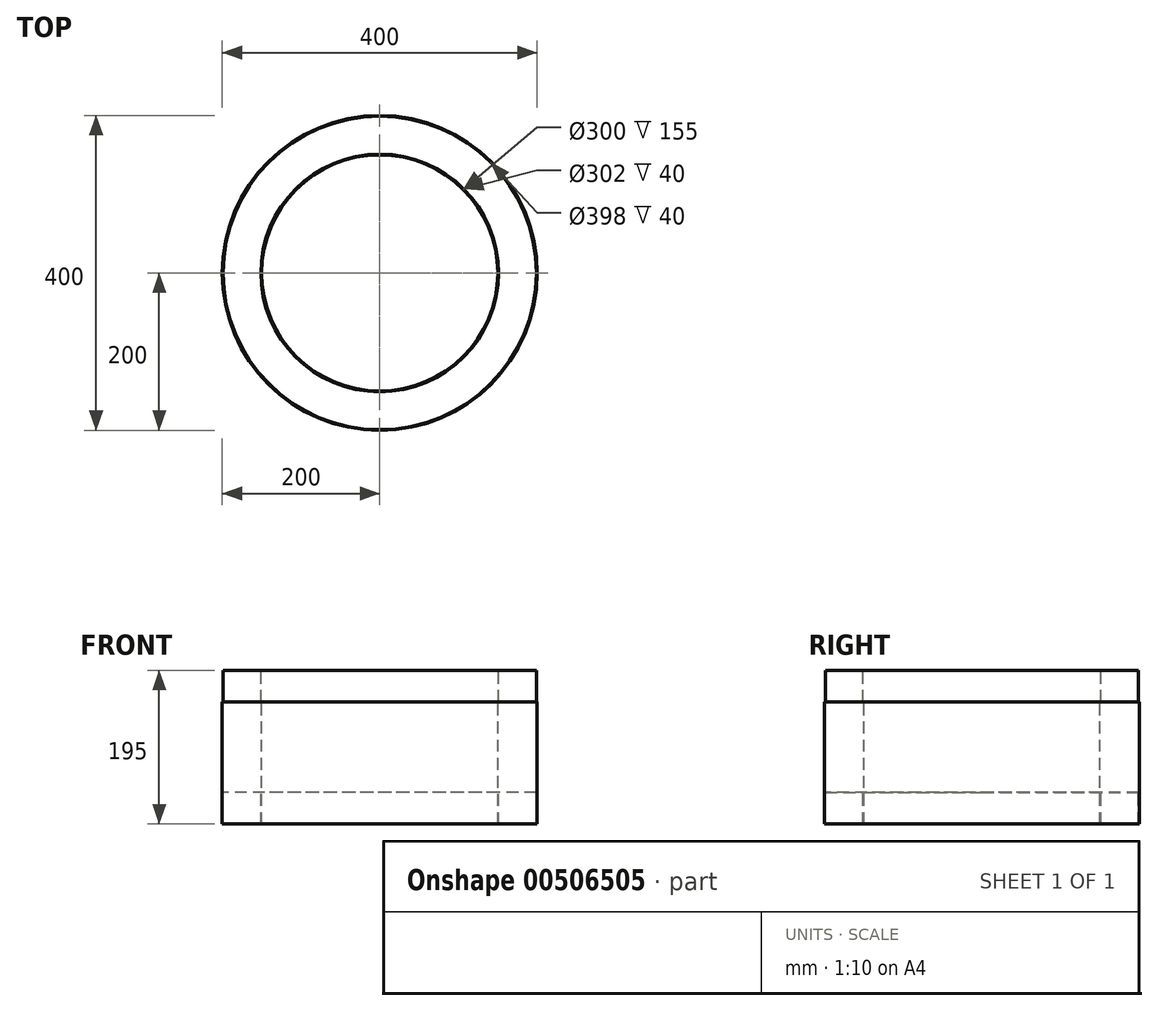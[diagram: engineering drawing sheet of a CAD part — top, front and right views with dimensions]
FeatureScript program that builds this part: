
annotation { "Feature Type Name" : "Feature", "Feature Type Description" : "" }
export const myFeature = defineFeature(function(context is Context, id is Id, definition is map)
    precondition{}
    {
        {
            var Q0;
            Q0=qCreatedBy(makeId("Front.planeOp"),FACE);
            var sketch = newSketch(context, id + "F0", { "sketchPlane" : qUnion([Q0])});
            skLineSegment(sketch, "E0", {"start": v(0, 74.87) * mm, "end": v(0, -73.71) * mm, "construction": true});
            skLineSegment(sketch, "E1", {"start": v(0, 374.84) * mm, "end": v(0, -528.94) * mm, "construction": true});
            skLineSegment(sketch, "E2", {"start": v(-150, -489.75) * mm, "end": v(-150, -334.75) * mm});
            skLineSegment(sketch, "E3", {"start": v(-150, -334.75) * mm, "end": v(-151, -334.75) * mm});
            skLineSegment(sketch, "E4", {"start": v(-151, -334.75) * mm, "end": v(-151, -294.75) * mm});
            skLineSegment(sketch, "E5", {"start": v(-151, -294.75) * mm, "end": v(-199, -294.75) * mm});
            skLineSegment(sketch, "E6", {"start": v(-199, -294.75) * mm, "end": v(-199, -334.75) * mm});
            skLineSegment(sketch, "E7", {"start": v(-199, -334.75) * mm, "end": v(-200, -334.75) * mm});
            skLineSegment(sketch, "E8", {"start": v(-200, -334.75) * mm, "end": v(-200, -489.75) * mm});
            skLineSegment(sketch, "E9", {"start": v(-200, -489.75) * mm, "end": v(-199, -489.75) * mm});
            skLineSegment(sketch, "E10", {"start": v(-199, -489.75) * mm, "end": v(-199, -449.75) * mm});
            skLineSegment(sketch, "E11", {"start": v(-199, -449.75) * mm, "end": v(-151, -449.75) * mm});
            skLineSegment(sketch, "E12", {"start": v(-151, -449.75) * mm, "end": v(-151, -489.75) * mm});
            skLineSegment(sketch, "E13", {"start": v(-151, -489.75) * mm, "end": v(-150, -489.75) * mm});
            skSolve(sketch);
        }
        {
            var Q0;
            Q0=qSketchRegion(id+"F0",true);
            var Q1;
            Q1=sQuery(id+"F0.wireOp",EDGE,"E1");
            revolve(context, id + "F1", {"entities" : qUnion([Q0]), "axis" : qUnion([Q1]), "revolveType" : RevolveType.FULL});
        }
    });
